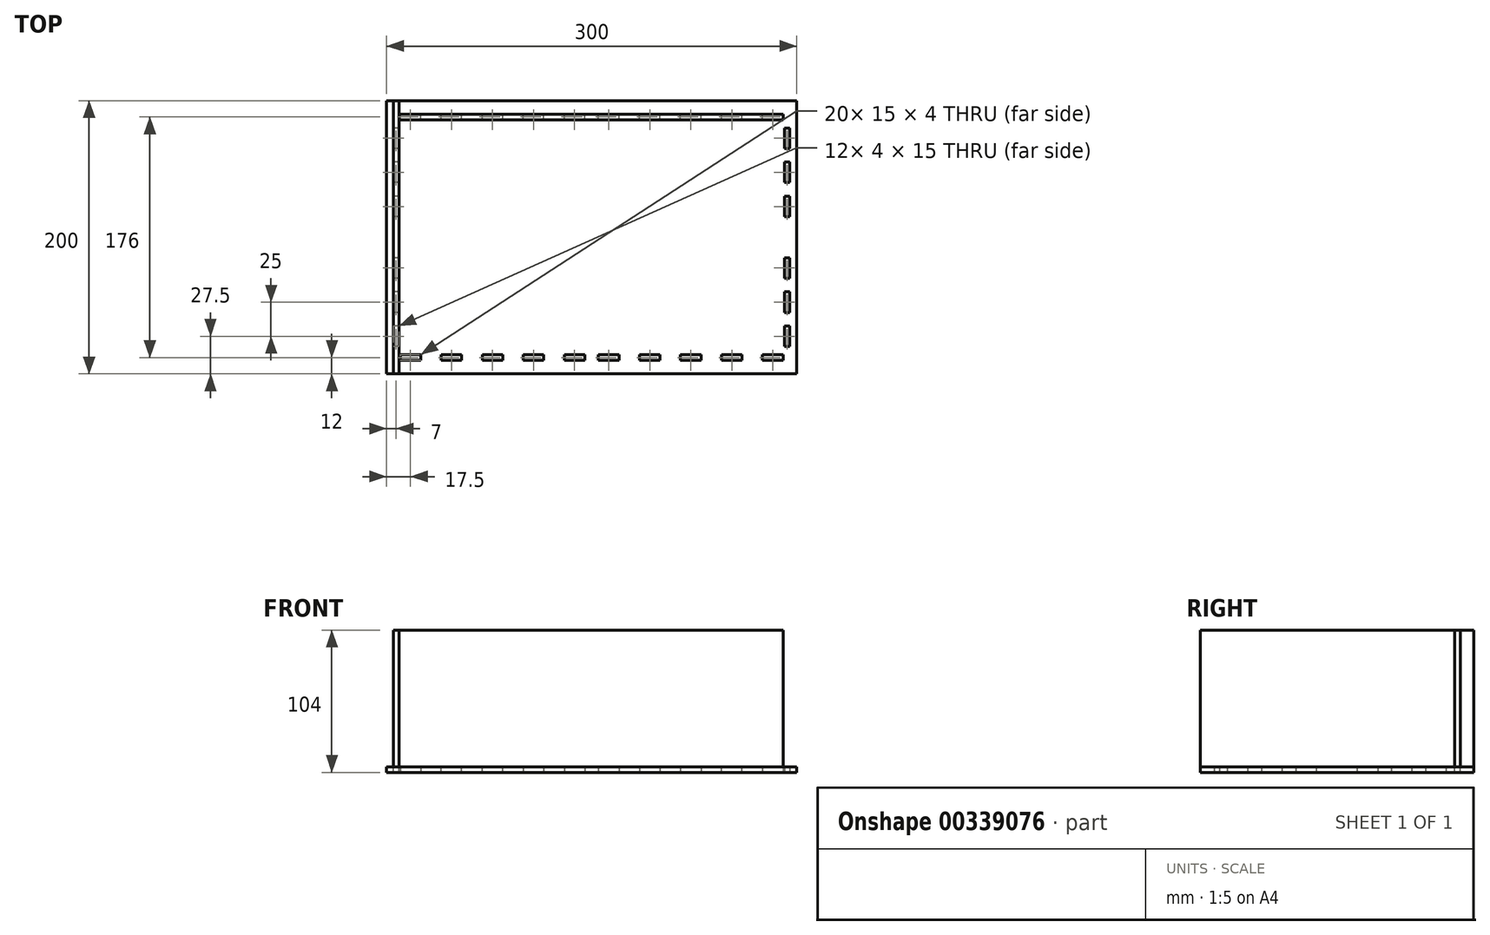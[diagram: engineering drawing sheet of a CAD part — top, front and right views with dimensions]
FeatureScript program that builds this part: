
annotation { "Feature Type Name" : "Feature", "Feature Type Description" : "" }
export const myFeature = defineFeature(function(context is Context, id is Id, definition is map)
    precondition{}
    {
        {
            assignVariable(context, id + "F0", {"name" : "material_thickness", "anyValue" : 4});
        }
        {
            var Q0;
            Q0=qCreatedBy(makeId("Top.planeOp"),FACE);
            var sketch = newSketch(context, id + "F1", { "sketchPlane" : qUnion([Q0])});
            skLineSegment(sketch, "E0.bottom", {"start": v(150, -100) * mm, "end": v(-150, -100) * mm});
            skLineSegment(sketch, "E0.top", {"start": v(150, 100) * mm, "end": v(-150, 100) * mm});
            skLineSegment(sketch, "E0.left", {"start": v(150, -100) * mm, "end": v(150, 100) * mm});
            skLineSegment(sketch, "E0.right", {"start": v(-150, -100) * mm, "end": v(-150, 100) * mm});
            skPoint(sketch, "E0.middle", {"position": v(0, 0) * mm});
            skLineSegment(sketch, "E1", {"start": v(0, 176.5) * mm, "end": v(0, -168.45) * mm, "construction": true});
            skPoint(sketch, "E1.endSnap0", {"position": v(0, -100) * mm});
            skLineSegment(sketch, "E2", {"start": v(-207.53, 0) * mm, "end": v(211.83, 0) * mm, "construction": true});
            skPoint(sketch, "E2.endSnap0", {"position": v(150, 0) * mm});
            skLineSegment(sketch, "E3.bottom", {"start": v(-125, 86) * mm, "end": v(-140, 86) * mm});
            skLineSegment(sketch, "E3.top", {"start": v(-125, 90) * mm, "end": v(-140, 90) * mm});
            skLineSegment(sketch, "E3.left", {"start": v(-125, 86) * mm, "end": v(-125, 90) * mm});
            skLineSegment(sketch, "E3.right", {"start": v(-140, 86) * mm, "end": v(-140, 90) * mm});
            skLineSegment(sketch, "E4.1.0.0", {"start": v(-95, 90) * mm, "end": v(-110, 90) * mm});
            skLineSegment(sketch, "E4.1.0.1", {"start": v(-110, 86) * mm, "end": v(-110, 90) * mm});
            skLineSegment(sketch, "E4.1.0.2", {"start": v(-95, 86) * mm, "end": v(-110, 86) * mm});
            skLineSegment(sketch, "E4.1.0.3", {"start": v(-95, 86) * mm, "end": v(-95, 90) * mm});
            skLineSegment(sketch, "E4.2.0.0", {"start": v(-65, 90) * mm, "end": v(-80, 90) * mm});
            skLineSegment(sketch, "E4.2.0.1", {"start": v(-80, 86) * mm, "end": v(-80, 90) * mm});
            skLineSegment(sketch, "E4.2.0.2", {"start": v(-65, 86) * mm, "end": v(-80, 86) * mm});
            skLineSegment(sketch, "E4.2.0.3", {"start": v(-65, 86) * mm, "end": v(-65, 90) * mm});
            skLineSegment(sketch, "E4.3.0.0", {"start": v(-35, 90) * mm, "end": v(-50, 90) * mm});
            skLineSegment(sketch, "E4.3.0.1", {"start": v(-50, 86) * mm, "end": v(-50, 90) * mm});
            skLineSegment(sketch, "E4.3.0.2", {"start": v(-35, 86) * mm, "end": v(-50, 86) * mm});
            skLineSegment(sketch, "E4.3.0.3", {"start": v(-35, 86) * mm, "end": v(-35, 90) * mm});
            skLineSegment(sketch, "E4.4.0.0", {"start": v(-5, 90) * mm, "end": v(-20, 90) * mm});
            skLineSegment(sketch, "E4.4.0.1", {"start": v(-20, 86) * mm, "end": v(-20, 90) * mm});
            skLineSegment(sketch, "E4.4.0.2", {"start": v(-5, 86) * mm, "end": v(-20, 86) * mm});
            skLineSegment(sketch, "E4.4.0.3", {"start": v(-5, 86) * mm, "end": v(-5, 90) * mm});
            skLineSegment(sketch, "E4.direction1", {"start": v(-140, 90) * mm, "end": v(-110, 90) * mm, "construction": true});
            skLineSegment(sketch, "E5.MirrorCS", {"start": v(5, 90) * mm, "end": v(20, 90) * mm});
            skLineSegment(sketch, "E6.MirrorCS", {"start": v(5, 86) * mm, "end": v(20, 86) * mm});
            skLineSegment(sketch, "E7.MirrorCS", {"start": v(5, 86) * mm, "end": v(5, 90) * mm});
            skLineSegment(sketch, "E8.MirrorCS", {"start": v(20, 86) * mm, "end": v(20, 90) * mm});
            skLineSegment(sketch, "E9.MirrorCS", {"start": v(110, 86) * mm, "end": v(110, 90) * mm});
            skLineSegment(sketch, "E10.MirrorCS", {"start": v(125, 86) * mm, "end": v(125, 90) * mm});
            skLineSegment(sketch, "E11.MirrorCS", {"start": v(50, 86) * mm, "end": v(50, 90) * mm});
            skLineSegment(sketch, "E12.MirrorCS", {"start": v(140, 86) * mm, "end": v(140, 90) * mm});
            skLineSegment(sketch, "E13.MirrorCS", {"start": v(95, 86) * mm, "end": v(95, 90) * mm});
            skLineSegment(sketch, "E14.MirrorCS", {"start": v(35, 86) * mm, "end": v(35, 90) * mm});
            skLineSegment(sketch, "E15.MirrorCS", {"start": v(80, 86) * mm, "end": v(80, 90) * mm});
            skLineSegment(sketch, "E16.MirrorCS", {"start": v(65, 86) * mm, "end": v(65, 90) * mm});
            skLineSegment(sketch, "E17.MirrorCS", {"start": v(125, 90) * mm, "end": v(140, 90) * mm});
            skLineSegment(sketch, "E18.MirrorCS", {"start": v(35, 86) * mm, "end": v(50, 86) * mm});
            skLineSegment(sketch, "E19.MirrorCS", {"start": v(95, 90) * mm, "end": v(110, 90) * mm});
            skLineSegment(sketch, "E20.MirrorCS", {"start": v(65, 86) * mm, "end": v(80, 86) * mm});
            skLineSegment(sketch, "E21.MirrorCS", {"start": v(95, 86) * mm, "end": v(110, 86) * mm});
            skLineSegment(sketch, "E22.MirrorCS", {"start": v(140, 90) * mm, "end": v(110, 90) * mm, "construction": true});
            skLineSegment(sketch, "E23.MirrorCS", {"start": v(65, 90) * mm, "end": v(80, 90) * mm});
            skLineSegment(sketch, "E24.MirrorCS", {"start": v(125, 86) * mm, "end": v(140, 86) * mm});
            skLineSegment(sketch, "E25.MirrorCS", {"start": v(35, 90) * mm, "end": v(50, 90) * mm});
            skLineSegment(sketch, "E26.bottom", {"start": v(141, 80) * mm, "end": v(145, 80) * mm});
            skLineSegment(sketch, "E26.top", {"start": v(141, 65) * mm, "end": v(145, 65) * mm});
            skLineSegment(sketch, "E26.left", {"start": v(141, 80) * mm, "end": v(141, 65) * mm});
            skLineSegment(sketch, "E26.right", {"start": v(145, 80) * mm, "end": v(145, 65) * mm});
            skLineSegment(sketch, "E27.0.1.0", {"start": v(145, 55) * mm, "end": v(145, 40) * mm});
            skLineSegment(sketch, "E27.0.1.1", {"start": v(141, 55) * mm, "end": v(145, 55) * mm});
            skLineSegment(sketch, "E27.0.1.2", {"start": v(141, 55) * mm, "end": v(141, 40) * mm});
            skLineSegment(sketch, "E27.0.1.3", {"start": v(141, 40) * mm, "end": v(145, 40) * mm});
            skLineSegment(sketch, "E27.0.2.0", {"start": v(145, 30) * mm, "end": v(145, 15) * mm});
            skLineSegment(sketch, "E27.0.2.1", {"start": v(141, 30) * mm, "end": v(145, 30) * mm});
            skLineSegment(sketch, "E27.0.2.2", {"start": v(141, 30) * mm, "end": v(141, 15) * mm});
            skLineSegment(sketch, "E27.0.2.3", {"start": v(141, 15) * mm, "end": v(145, 15) * mm});
            skLineSegment(sketch, "E27.direction1", {"start": v(145, 65) * mm, "end": v(170, 65) * mm, "construction": true});
            skLineSegment(sketch, "E27.direction2", {"start": v(145, 65) * mm, "end": v(145, 40) * mm, "construction": true});
            skLineSegment(sketch, "E28.MirrorCS", {"start": v(141, -55) * mm, "end": v(141, -40) * mm});
            skLineSegment(sketch, "E29.MirrorCS", {"start": v(141, -40) * mm, "end": v(145, -40) * mm});
            skLineSegment(sketch, "E30.MirrorCS", {"start": v(141, -30) * mm, "end": v(145, -30) * mm});
            skLineSegment(sketch, "E31.MirrorCS", {"start": v(145, -30) * mm, "end": v(145, -15) * mm});
            skLineSegment(sketch, "E32.MirrorCS", {"start": v(141, -30) * mm, "end": v(141, -15) * mm});
            skLineSegment(sketch, "E33.MirrorCS", {"start": v(141, -15) * mm, "end": v(145, -15) * mm});
            skLineSegment(sketch, "E34.MirrorCS", {"start": v(141, -55) * mm, "end": v(145, -55) * mm});
            skLineSegment(sketch, "E35.MirrorCS", {"start": v(141, -65) * mm, "end": v(145, -65) * mm});
            skLineSegment(sketch, "E36.MirrorCS", {"start": v(145, -80) * mm, "end": v(145, -65) * mm});
            skLineSegment(sketch, "E37.MirrorCS", {"start": v(141, -80) * mm, "end": v(141, -65) * mm});
            skLineSegment(sketch, "E38.MirrorCS", {"start": v(141, -80) * mm, "end": v(145, -80) * mm});
            skLineSegment(sketch, "E39.MirrorCS", {"start": v(145, -55) * mm, "end": v(145, -40) * mm});
            skLineSegment(sketch, "E40.MirrorCS", {"start": v(140, -86) * mm, "end": v(140, -90) * mm});
            skLineSegment(sketch, "E41.MirrorCS", {"start": v(125, -86) * mm, "end": v(140, -86) * mm});
            skLineSegment(sketch, "E42.MirrorCS", {"start": v(125, -86) * mm, "end": v(125, -90) * mm});
            skLineSegment(sketch, "E43.MirrorCS", {"start": v(125, -90) * mm, "end": v(140, -90) * mm});
            skLineSegment(sketch, "E44.MirrorCS", {"start": v(110, -86) * mm, "end": v(110, -90) * mm});
            skLineSegment(sketch, "E45.MirrorCS", {"start": v(95, -90) * mm, "end": v(110, -90) * mm});
            skLineSegment(sketch, "E46.MirrorCS", {"start": v(95, -86) * mm, "end": v(95, -90) * mm});
            skLineSegment(sketch, "E47.MirrorCS", {"start": v(95, -86) * mm, "end": v(110, -86) * mm});
            skLineSegment(sketch, "E48.MirrorCS", {"start": v(80, -86) * mm, "end": v(80, -90) * mm});
            skLineSegment(sketch, "E49.MirrorCS", {"start": v(65, -90) * mm, "end": v(80, -90) * mm});
            skLineSegment(sketch, "E50.MirrorCS", {"start": v(65, -86) * mm, "end": v(65, -90) * mm});
            skLineSegment(sketch, "E51.MirrorCS", {"start": v(65, -86) * mm, "end": v(80, -86) * mm});
            skLineSegment(sketch, "E52.MirrorCS", {"start": v(50, -86) * mm, "end": v(50, -90) * mm});
            skLineSegment(sketch, "E53.MirrorCS", {"start": v(35, -90) * mm, "end": v(50, -90) * mm});
            skLineSegment(sketch, "E54.MirrorCS", {"start": v(35, -86) * mm, "end": v(50, -86) * mm});
            skLineSegment(sketch, "E55.MirrorCS", {"start": v(35, -86) * mm, "end": v(35, -90) * mm});
            skLineSegment(sketch, "E56.MirrorCS", {"start": v(20, -86) * mm, "end": v(20, -90) * mm});
            skLineSegment(sketch, "E57.MirrorCS", {"start": v(5, -90) * mm, "end": v(20, -90) * mm});
            skLineSegment(sketch, "E58.MirrorCS", {"start": v(5, -86) * mm, "end": v(20, -86) * mm});
            skLineSegment(sketch, "E59.MirrorCS", {"start": v(5, -86) * mm, "end": v(5, -90) * mm});
            skLineSegment(sketch, "E60.MirrorCS", {"start": v(-5, -86) * mm, "end": v(-5, -90) * mm});
            skLineSegment(sketch, "E61.MirrorCS", {"start": v(-5, -90) * mm, "end": v(-20, -90) * mm});
            skLineSegment(sketch, "E62.MirrorCS", {"start": v(-5, -86) * mm, "end": v(-20, -86) * mm});
            skLineSegment(sketch, "E63.MirrorCS", {"start": v(-20, -86) * mm, "end": v(-20, -90) * mm});
            skLineSegment(sketch, "E64.MirrorCS", {"start": v(-35, -86) * mm, "end": v(-35, -90) * mm});
            skLineSegment(sketch, "E65.MirrorCS", {"start": v(-35, -90) * mm, "end": v(-50, -90) * mm});
            skLineSegment(sketch, "E66.MirrorCS", {"start": v(-35, -86) * mm, "end": v(-50, -86) * mm});
            skLineSegment(sketch, "E67.MirrorCS", {"start": v(-50, -86) * mm, "end": v(-50, -90) * mm});
            skLineSegment(sketch, "E68.MirrorCS", {"start": v(-65, -86) * mm, "end": v(-65, -90) * mm});
            skLineSegment(sketch, "E69.MirrorCS", {"start": v(-65, -90) * mm, "end": v(-80, -90) * mm});
            skLineSegment(sketch, "E70.MirrorCS", {"start": v(-65, -86) * mm, "end": v(-80, -86) * mm});
            skLineSegment(sketch, "E71.MirrorCS", {"start": v(-80, -86) * mm, "end": v(-80, -90) * mm});
            skLineSegment(sketch, "E72.MirrorCS", {"start": v(-95, -86) * mm, "end": v(-95, -90) * mm});
            skLineSegment(sketch, "E73.MirrorCS", {"start": v(-95, -90) * mm, "end": v(-110, -90) * mm});
            skLineSegment(sketch, "E74.MirrorCS", {"start": v(-95, -86) * mm, "end": v(-110, -86) * mm});
            skLineSegment(sketch, "E75.MirrorCS", {"start": v(-110, -86) * mm, "end": v(-110, -90) * mm});
            skLineSegment(sketch, "E76.MirrorCS", {"start": v(-125, -86) * mm, "end": v(-125, -90) * mm});
            skLineSegment(sketch, "E77.MirrorCS", {"start": v(-125, -86) * mm, "end": v(-140, -86) * mm});
            skLineSegment(sketch, "E78.MirrorCS", {"start": v(-140, -86) * mm, "end": v(-140, -90) * mm});
            skLineSegment(sketch, "E79.MirrorCS", {"start": v(-125, -90) * mm, "end": v(-140, -90) * mm});
            skLineSegment(sketch, "E80.MirrorCS", {"start": v(-141, 80) * mm, "end": v(-145, 80) * mm});
            skLineSegment(sketch, "E81.MirrorCS", {"start": v(-141, 80) * mm, "end": v(-141, 65) * mm});
            skLineSegment(sketch, "E82.MirrorCS", {"start": v(-145, 80) * mm, "end": v(-145, 65) * mm});
            skLineSegment(sketch, "E83.MirrorCS", {"start": v(-141, 65) * mm, "end": v(-145, 65) * mm});
            skLineSegment(sketch, "E84.MirrorCS", {"start": v(-141, 55) * mm, "end": v(-141, 40) * mm});
            skLineSegment(sketch, "E85.MirrorCS", {"start": v(-141, 40) * mm, "end": v(-145, 40) * mm});
            skLineSegment(sketch, "E86.MirrorCS", {"start": v(-141, 55) * mm, "end": v(-145, 55) * mm});
            skLineSegment(sketch, "E87.MirrorCS", {"start": v(-145, 55) * mm, "end": v(-145, 40) * mm});
            skLineSegment(sketch, "E88.MirrorCS", {"start": v(-141, 30) * mm, "end": v(-145, 30) * mm});
            skLineSegment(sketch, "E89.MirrorCS", {"start": v(-141, 30) * mm, "end": v(-141, 15) * mm});
            skLineSegment(sketch, "E90.MirrorCS", {"start": v(-145, 30) * mm, "end": v(-145, 15) * mm});
            skLineSegment(sketch, "E91.MirrorCS", {"start": v(-141, 15) * mm, "end": v(-145, 15) * mm});
            skLineSegment(sketch, "E92.MirrorCS", {"start": v(-141, -30) * mm, "end": v(-141, -15) * mm});
            skLineSegment(sketch, "E93.MirrorCS", {"start": v(-145, -30) * mm, "end": v(-145, -15) * mm});
            skLineSegment(sketch, "E94.MirrorCS", {"start": v(-141, -30) * mm, "end": v(-145, -30) * mm});
            skLineSegment(sketch, "E95.MirrorCS", {"start": v(-141, -15) * mm, "end": v(-145, -15) * mm});
            skLineSegment(sketch, "E96.MirrorCS", {"start": v(-145, -55) * mm, "end": v(-145, -40) * mm});
            skLineSegment(sketch, "E97.MirrorCS", {"start": v(-141, -55) * mm, "end": v(-141, -40) * mm});
            skLineSegment(sketch, "E98.MirrorCS", {"start": v(-141, -55) * mm, "end": v(-145, -55) * mm});
            skLineSegment(sketch, "E99.MirrorCS", {"start": v(-141, -40) * mm, "end": v(-145, -40) * mm});
            skLineSegment(sketch, "E100.MirrorCS", {"start": v(-141, -65) * mm, "end": v(-145, -65) * mm});
            skLineSegment(sketch, "E101.MirrorCS", {"start": v(-141, -80) * mm, "end": v(-141, -65) * mm});
            skLineSegment(sketch, "E102.MirrorCS", {"start": v(-145, -80) * mm, "end": v(-145, -65) * mm});
            skLineSegment(sketch, "E103.MirrorCS", {"start": v(-141, -80) * mm, "end": v(-145, -80) * mm});
            skSolve(sketch);
        }
        {
            var Q0;
            Q0=makeQuery(id+"F1.imprint","IMPRINT",FACE,{"disambiguationData":[TD([[makeQuery(id+"F1.imprint","IMPRINT",EDGE,{"derivedFrom":sQuery(id+"F1.wireOp",EDGE,"E0.bottom")}),-1.0]])]});
            extrude(context, id + "F2", {"entities" : qUnion([Q0]), "depth" : (getVariable(context, 'material_thickness')) * mm});
        }
        {
            var Q0;
            Q0=makeQuery(id+"F2.opExtrude","CAP_FACE",FACE,{"disambiguationData":[OSD([sQuery(id+"F1.wireOp",EDGE,"E0.bottom"),sQuery(id+"F1.wireOp",EDGE,"E0.top"),sQuery(id+"F1.wireOp",EDGE,"E0.left"),sQuery(id+"F1.wireOp",EDGE,"E0.right"),sQuery(id+"F1.wireOp",EDGE,"E3.bottom"),sQuery(id+"F1.wireOp",EDGE,"E3.top"),sQuery(id+"F1.wireOp",EDGE,"E3.left"),sQuery(id+"F1.wireOp",EDGE,"E3.right"),sQuery(id+"F1.wireOp",EDGE,"E4.1.0.0"),sQuery(id+"F1.wireOp",EDGE,"E4.1.0.1"),sQuery(id+"F1.wireOp",EDGE,"E4.1.0.2"),sQuery(id+"F1.wireOp",EDGE,"E4.1.0.3"),sQuery(id+"F1.wireOp",EDGE,"E4.2.0.0"),sQuery(id+"F1.wireOp",EDGE,"E4.2.0.1"),sQuery(id+"F1.wireOp",EDGE,"E4.2.0.2"),sQuery(id+"F1.wireOp",EDGE,"E4.2.0.3"),sQuery(id+"F1.wireOp",EDGE,"E4.3.0.0"),sQuery(id+"F1.wireOp",EDGE,"E4.3.0.1"),sQuery(id+"F1.wireOp",EDGE,"E4.3.0.2"),sQuery(id+"F1.wireOp",EDGE,"E4.3.0.3"),sQuery(id+"F1.wireOp",EDGE,"E4.4.0.0"),sQuery(id+"F1.wireOp",EDGE,"E4.4.0.1"),sQuery(id+"F1.wireOp",EDGE,"E4.4.0.2"),sQuery(id+"F1.wireOp",EDGE,"E4.4.0.3"),sQuery(id+"F1.wireOp",EDGE,"E5.MirrorCS"),sQuery(id+"F1.wireOp",EDGE,"E6.MirrorCS"),sQuery(id+"F1.wireOp",EDGE,"E7.MirrorCS"),sQuery(id+"F1.wireOp",EDGE,"E8.MirrorCS"),sQuery(id+"F1.wireOp",EDGE,"E9.MirrorCS"),sQuery(id+"F1.wireOp",EDGE,"E10.MirrorCS"),sQuery(id+"F1.wireOp",EDGE,"E11.MirrorCS"),sQuery(id+"F1.wireOp",EDGE,"E12.MirrorCS"),sQuery(id+"F1.wireOp",EDGE,"E13.MirrorCS"),sQuery(id+"F1.wireOp",EDGE,"E14.MirrorCS"),sQuery(id+"F1.wireOp",EDGE,"E15.MirrorCS"),sQuery(id+"F1.wireOp",EDGE,"E16.MirrorCS"),sQuery(id+"F1.wireOp",EDGE,"E17.MirrorCS"),sQuery(id+"F1.wireOp",EDGE,"E18.MirrorCS"),sQuery(id+"F1.wireOp",EDGE,"E19.MirrorCS"),sQuery(id+"F1.wireOp",EDGE,"E20.MirrorCS"),sQuery(id+"F1.wireOp",EDGE,"E21.MirrorCS"),sQuery(id+"F1.wireOp",EDGE,"E23.MirrorCS"),sQuery(id+"F1.wireOp",EDGE,"E24.MirrorCS"),sQuery(id+"F1.wireOp",EDGE,"E25.MirrorCS"),sQuery(id+"F1.wireOp",EDGE,"E26.bottom"),sQuery(id+"F1.wireOp",EDGE,"E26.top"),sQuery(id+"F1.wireOp",EDGE,"E26.left"),sQuery(id+"F1.wireOp",EDGE,"E26.right"),sQuery(id+"F1.wireOp",EDGE,"E27.0.1.0"),sQuery(id+"F1.wireOp",EDGE,"E27.0.1.1"),sQuery(id+"F1.wireOp",EDGE,"E27.0.1.2"),sQuery(id+"F1.wireOp",EDGE,"E27.0.1.3"),sQuery(id+"F1.wireOp",EDGE,"E27.0.2.0"),sQuery(id+"F1.wireOp",EDGE,"E27.0.2.1"),sQuery(id+"F1.wireOp",EDGE,"E27.0.2.2"),sQuery(id+"F1.wireOp",EDGE,"E27.0.2.3"),sQuery(id+"F1.wireOp",EDGE,"E28.MirrorCS"),sQuery(id+"F1.wireOp",EDGE,"E30.MirrorCS"),sQuery(id+"F1.wireOp",EDGE,"E31.MirrorCS"),sQuery(id+"F1.wireOp",EDGE,"E32.MirrorCS"),sQuery(id+"F1.wireOp",EDGE,"E33.MirrorCS"),sQuery(id+"F1.wireOp",EDGE,"E29.MirrorCS"),sQuery(id+"F1.wireOp",EDGE,"E34.MirrorCS"),sQuery(id+"F1.wireOp",EDGE,"E35.MirrorCS"),sQuery(id+"F1.wireOp",EDGE,"E36.MirrorCS"),sQuery(id+"F1.wireOp",EDGE,"E37.MirrorCS"),sQuery(id+"F1.wireOp",EDGE,"E38.MirrorCS"),sQuery(id+"F1.wireOp",EDGE,"E39.MirrorCS"),sQuery(id+"F1.wireOp",EDGE,"E40.MirrorCS"),sQuery(id+"F1.wireOp",EDGE,"E41.MirrorCS"),sQuery(id+"F1.wireOp",EDGE,"E42.MirrorCS"),sQuery(id+"F1.wireOp",EDGE,"E43.MirrorCS"),sQuery(id+"F1.wireOp",EDGE,"E44.MirrorCS"),sQuery(id+"F1.wireOp",EDGE,"E45.MirrorCS"),sQuery(id+"F1.wireOp",EDGE,"E46.MirrorCS"),sQuery(id+"F1.wireOp",EDGE,"E47.MirrorCS"),sQuery(id+"F1.wireOp",EDGE,"E48.MirrorCS"),sQuery(id+"F1.wireOp",EDGE,"E49.MirrorCS"),sQuery(id+"F1.wireOp",EDGE,"E50.MirrorCS"),sQuery(id+"F1.wireOp",EDGE,"E51.MirrorCS"),sQuery(id+"F1.wireOp",EDGE,"E52.MirrorCS"),sQuery(id+"F1.wireOp",EDGE,"E53.MirrorCS"),sQuery(id+"F1.wireOp",EDGE,"E54.MirrorCS"),sQuery(id+"F1.wireOp",EDGE,"E55.MirrorCS"),sQuery(id+"F1.wireOp",EDGE,"E56.MirrorCS"),sQuery(id+"F1.wireOp",EDGE,"E57.MirrorCS"),sQuery(id+"F1.wireOp",EDGE,"E58.MirrorCS"),sQuery(id+"F1.wireOp",EDGE,"E59.MirrorCS"),sQuery(id+"F1.wireOp",EDGE,"E60.MirrorCS"),sQuery(id+"F1.wireOp",EDGE,"E61.MirrorCS"),sQuery(id+"F1.wireOp",EDGE,"E62.MirrorCS"),sQuery(id+"F1.wireOp",EDGE,"E63.MirrorCS"),sQuery(id+"F1.wireOp",EDGE,"E64.MirrorCS"),sQuery(id+"F1.wireOp",EDGE,"E65.MirrorCS"),sQuery(id+"F1.wireOp",EDGE,"E66.MirrorCS"),sQuery(id+"F1.wireOp",EDGE,"E67.MirrorCS"),sQuery(id+"F1.wireOp",EDGE,"E68.MirrorCS"),sQuery(id+"F1.wireOp",EDGE,"E69.MirrorCS"),sQuery(id+"F1.wireOp",EDGE,"E70.MirrorCS"),sQuery(id+"F1.wireOp",EDGE,"E71.MirrorCS"),sQuery(id+"F1.wireOp",EDGE,"E72.MirrorCS"),sQuery(id+"F1.wireOp",EDGE,"E73.MirrorCS"),sQuery(id+"F1.wireOp",EDGE,"E74.MirrorCS"),sQuery(id+"F1.wireOp",EDGE,"E75.MirrorCS"),sQuery(id+"F1.wireOp",EDGE,"E76.MirrorCS"),sQuery(id+"F1.wireOp",EDGE,"E77.MirrorCS"),sQuery(id+"F1.wireOp",EDGE,"E78.MirrorCS"),sQuery(id+"F1.wireOp",EDGE,"E79.MirrorCS"),sQuery(id+"F1.wireOp",EDGE,"E80.MirrorCS"),sQuery(id+"F1.wireOp",EDGE,"E81.MirrorCS"),sQuery(id+"F1.wireOp",EDGE,"E82.MirrorCS"),sQuery(id+"F1.wireOp",EDGE,"E83.MirrorCS"),sQuery(id+"F1.wireOp",EDGE,"E84.MirrorCS"),sQuery(id+"F1.wireOp",EDGE,"E85.MirrorCS"),sQuery(id+"F1.wireOp",EDGE,"E86.MirrorCS"),sQuery(id+"F1.wireOp",EDGE,"E87.MirrorCS"),sQuery(id+"F1.wireOp",EDGE,"E88.MirrorCS"),sQuery(id+"F1.wireOp",EDGE,"E89.MirrorCS"),sQuery(id+"F1.wireOp",EDGE,"E90.MirrorCS"),sQuery(id+"F1.wireOp",EDGE,"E91.MirrorCS"),sQuery(id+"F1.wireOp",EDGE,"E92.MirrorCS"),sQuery(id+"F1.wireOp",EDGE,"E93.MirrorCS"),sQuery(id+"F1.wireOp",EDGE,"E94.MirrorCS"),sQuery(id+"F1.wireOp",EDGE,"E95.MirrorCS"),sQuery(id+"F1.wireOp",EDGE,"E96.MirrorCS"),sQuery(id+"F1.wireOp",EDGE,"E97.MirrorCS"),sQuery(id+"F1.wireOp",EDGE,"E98.MirrorCS"),sQuery(id+"F1.wireOp",EDGE,"E99.MirrorCS"),sQuery(id+"F1.wireOp",EDGE,"E100.MirrorCS"),sQuery(id+"F1.wireOp",EDGE,"E101.MirrorCS"),sQuery(id+"F1.wireOp",EDGE,"E102.MirrorCS"),sQuery(id+"F1.wireOp",EDGE,"E103.MirrorCS")])],"isStart":false});
            var sketch = newSketch(context, id + "F3", { "sketchPlane" : qUnion([Q0])});
            skLineSegment(sketch, "E104.bottom", {"start": v(-145, -80) * mm, "end": v(-141, -80) * mm});
            skLineSegment(sketch, "E104.top", {"start": v(-145, -65) * mm, "end": v(-141, -65) * mm});
            skLineSegment(sketch, "E104.left", {"start": v(-145, -80) * mm, "end": v(-145, -65) * mm});
            skLineSegment(sketch, "E104.right", {"start": v(-141, -80) * mm, "end": v(-141, -65) * mm});
            skLineSegment(sketch, "E105.bottom", {"start": v(-145, -55) * mm, "end": v(-141, -55) * mm});
            skLineSegment(sketch, "E105.top", {"start": v(-145, -40) * mm, "end": v(-141, -40) * mm});
            skLineSegment(sketch, "E105.left", {"start": v(-145, -55) * mm, "end": v(-145, -40) * mm});
            skLineSegment(sketch, "E105.right", {"start": v(-141, -55) * mm, "end": v(-141, -40) * mm});
            skLineSegment(sketch, "E106.bottom", {"start": v(-145, -30) * mm, "end": v(-141, -30) * mm});
            skLineSegment(sketch, "E106.top", {"start": v(-145, -15) * mm, "end": v(-141, -15) * mm});
            skLineSegment(sketch, "E106.left", {"start": v(-145, -30) * mm, "end": v(-145, -15) * mm});
            skLineSegment(sketch, "E106.right", {"start": v(-141, -30) * mm, "end": v(-141, -15) * mm});
            skLineSegment(sketch, "E107.bottom", {"start": v(-145, 15) * mm, "end": v(-141, 15) * mm});
            skLineSegment(sketch, "E107.top", {"start": v(-145, 30) * mm, "end": v(-141, 30) * mm});
            skLineSegment(sketch, "E107.left", {"start": v(-145, 15) * mm, "end": v(-145, 30) * mm});
            skLineSegment(sketch, "E107.right", {"start": v(-141, 15) * mm, "end": v(-141, 30) * mm});
            skLineSegment(sketch, "E108.bottom", {"start": v(-145, 40) * mm, "end": v(-141, 40) * mm});
            skLineSegment(sketch, "E108.top", {"start": v(-145, 55) * mm, "end": v(-141, 55) * mm});
            skLineSegment(sketch, "E108.left", {"start": v(-145, 40) * mm, "end": v(-145, 55) * mm});
            skLineSegment(sketch, "E108.right", {"start": v(-141, 40) * mm, "end": v(-141, 55) * mm});
            skLineSegment(sketch, "E109.bottom", {"start": v(-145, 65) * mm, "end": v(-141, 65) * mm});
            skLineSegment(sketch, "E109.top", {"start": v(-145, 80) * mm, "end": v(-141, 80) * mm});
            skLineSegment(sketch, "E109.left", {"start": v(-145, 65) * mm, "end": v(-145, 80) * mm});
            skLineSegment(sketch, "E109.right", {"start": v(-141, 65) * mm, "end": v(-141, 80) * mm});
            skSolve(sketch);
        }
        {
            var Q0;
            Q0=makeQuery(id+"F3.imprint","IMPRINT",FACE,{"disambiguationData":[TD([[makeQuery(id+"F3.imprint","IMPRINT",EDGE,{"derivedFrom":sQuery(id+"F3.wireOp",EDGE,"E104.bottom")}),-1.0]])]});
            var Q1;
            Q1=makeQuery(id+"F3.imprint","IMPRINT",FACE,{"disambiguationData":[TD([[makeQuery(id+"F3.imprint","IMPRINT",EDGE,{"derivedFrom":sQuery(id+"F3.wireOp",EDGE,"E105.bottom")}),-1.0]])]});
            var Q2;
            Q2=makeQuery(id+"F3.imprint","IMPRINT",FACE,{"disambiguationData":[TD([[makeQuery(id+"F3.imprint","IMPRINT",EDGE,{"derivedFrom":sQuery(id+"F3.wireOp",EDGE,"E106.bottom")}),-1.0]])]});
            var Q3;
            Q3=makeQuery(id+"F3.imprint","IMPRINT",FACE,{"disambiguationData":[TD([[makeQuery(id+"F3.imprint","IMPRINT",EDGE,{"derivedFrom":sQuery(id+"F3.wireOp",EDGE,"E107.bottom")}),-1.0]])]});
            var Q4;
            Q4=makeQuery(id+"F3.imprint","IMPRINT",FACE,{"disambiguationData":[TD([[makeQuery(id+"F3.imprint","IMPRINT",EDGE,{"derivedFrom":sQuery(id+"F3.wireOp",EDGE,"E108.bottom")}),-1.0]])]});
            var Q5;
            Q5=makeQuery(id+"F3.imprint","IMPRINT",FACE,{"disambiguationData":[TD([[makeQuery(id+"F3.imprint","IMPRINT",EDGE,{"derivedFrom":sQuery(id+"F3.wireOp",EDGE,"E109.bottom")}),-1.0]])]});
            extrude(context, id + "F4", {"entities" : qUnion([Q0, Q1, Q2, Q3, Q4, Q5]), "oppositeDirection" : true, "depth" : 4 * mm});
        }
        {
            var Q0;
            Q0=makeQuery(id+"F2.opExtrude","CAP_FACE",FACE,{"disambiguationData":[OSD([sQuery(id+"F1.wireOp",EDGE,"E0.bottom"),sQuery(id+"F1.wireOp",EDGE,"E0.top"),sQuery(id+"F1.wireOp",EDGE,"E0.left"),sQuery(id+"F1.wireOp",EDGE,"E0.right"),sQuery(id+"F1.wireOp",EDGE,"E3.bottom"),sQuery(id+"F1.wireOp",EDGE,"E3.top"),sQuery(id+"F1.wireOp",EDGE,"E3.left"),sQuery(id+"F1.wireOp",EDGE,"E3.right"),sQuery(id+"F1.wireOp",EDGE,"E4.1.0.0"),sQuery(id+"F1.wireOp",EDGE,"E4.1.0.1"),sQuery(id+"F1.wireOp",EDGE,"E4.1.0.2"),sQuery(id+"F1.wireOp",EDGE,"E4.1.0.3"),sQuery(id+"F1.wireOp",EDGE,"E4.2.0.0"),sQuery(id+"F1.wireOp",EDGE,"E4.2.0.1"),sQuery(id+"F1.wireOp",EDGE,"E4.2.0.2"),sQuery(id+"F1.wireOp",EDGE,"E4.2.0.3"),sQuery(id+"F1.wireOp",EDGE,"E4.3.0.0"),sQuery(id+"F1.wireOp",EDGE,"E4.3.0.1"),sQuery(id+"F1.wireOp",EDGE,"E4.3.0.2"),sQuery(id+"F1.wireOp",EDGE,"E4.3.0.3"),sQuery(id+"F1.wireOp",EDGE,"E4.4.0.0"),sQuery(id+"F1.wireOp",EDGE,"E4.4.0.1"),sQuery(id+"F1.wireOp",EDGE,"E4.4.0.2"),sQuery(id+"F1.wireOp",EDGE,"E4.4.0.3"),sQuery(id+"F1.wireOp",EDGE,"E5.MirrorCS"),sQuery(id+"F1.wireOp",EDGE,"E6.MirrorCS"),sQuery(id+"F1.wireOp",EDGE,"E7.MirrorCS"),sQuery(id+"F1.wireOp",EDGE,"E8.MirrorCS"),sQuery(id+"F1.wireOp",EDGE,"E9.MirrorCS"),sQuery(id+"F1.wireOp",EDGE,"E10.MirrorCS"),sQuery(id+"F1.wireOp",EDGE,"E11.MirrorCS"),sQuery(id+"F1.wireOp",EDGE,"E12.MirrorCS"),sQuery(id+"F1.wireOp",EDGE,"E13.MirrorCS"),sQuery(id+"F1.wireOp",EDGE,"E14.MirrorCS"),sQuery(id+"F1.wireOp",EDGE,"E15.MirrorCS"),sQuery(id+"F1.wireOp",EDGE,"E16.MirrorCS"),sQuery(id+"F1.wireOp",EDGE,"E17.MirrorCS"),sQuery(id+"F1.wireOp",EDGE,"E18.MirrorCS"),sQuery(id+"F1.wireOp",EDGE,"E19.MirrorCS"),sQuery(id+"F1.wireOp",EDGE,"E20.MirrorCS"),sQuery(id+"F1.wireOp",EDGE,"E21.MirrorCS"),sQuery(id+"F1.wireOp",EDGE,"E23.MirrorCS"),sQuery(id+"F1.wireOp",EDGE,"E24.MirrorCS"),sQuery(id+"F1.wireOp",EDGE,"E25.MirrorCS"),sQuery(id+"F1.wireOp",EDGE,"E26.bottom"),sQuery(id+"F1.wireOp",EDGE,"E26.top"),sQuery(id+"F1.wireOp",EDGE,"E26.left"),sQuery(id+"F1.wireOp",EDGE,"E26.right"),sQuery(id+"F1.wireOp",EDGE,"E27.0.1.0"),sQuery(id+"F1.wireOp",EDGE,"E27.0.1.1"),sQuery(id+"F1.wireOp",EDGE,"E27.0.1.2"),sQuery(id+"F1.wireOp",EDGE,"E27.0.1.3"),sQuery(id+"F1.wireOp",EDGE,"E27.0.2.0"),sQuery(id+"F1.wireOp",EDGE,"E27.0.2.1"),sQuery(id+"F1.wireOp",EDGE,"E27.0.2.2"),sQuery(id+"F1.wireOp",EDGE,"E27.0.2.3"),sQuery(id+"F1.wireOp",EDGE,"E28.MirrorCS"),sQuery(id+"F1.wireOp",EDGE,"E30.MirrorCS"),sQuery(id+"F1.wireOp",EDGE,"E31.MirrorCS"),sQuery(id+"F1.wireOp",EDGE,"E32.MirrorCS"),sQuery(id+"F1.wireOp",EDGE,"E33.MirrorCS"),sQuery(id+"F1.wireOp",EDGE,"E29.MirrorCS"),sQuery(id+"F1.wireOp",EDGE,"E34.MirrorCS"),sQuery(id+"F1.wireOp",EDGE,"E35.MirrorCS"),sQuery(id+"F1.wireOp",EDGE,"E36.MirrorCS"),sQuery(id+"F1.wireOp",EDGE,"E37.MirrorCS"),sQuery(id+"F1.wireOp",EDGE,"E38.MirrorCS"),sQuery(id+"F1.wireOp",EDGE,"E39.MirrorCS"),sQuery(id+"F1.wireOp",EDGE,"E40.MirrorCS"),sQuery(id+"F1.wireOp",EDGE,"E41.MirrorCS"),sQuery(id+"F1.wireOp",EDGE,"E42.MirrorCS"),sQuery(id+"F1.wireOp",EDGE,"E43.MirrorCS"),sQuery(id+"F1.wireOp",EDGE,"E44.MirrorCS"),sQuery(id+"F1.wireOp",EDGE,"E45.MirrorCS"),sQuery(id+"F1.wireOp",EDGE,"E46.MirrorCS"),sQuery(id+"F1.wireOp",EDGE,"E47.MirrorCS"),sQuery(id+"F1.wireOp",EDGE,"E48.MirrorCS"),sQuery(id+"F1.wireOp",EDGE,"E49.MirrorCS"),sQuery(id+"F1.wireOp",EDGE,"E50.MirrorCS"),sQuery(id+"F1.wireOp",EDGE,"E51.MirrorCS"),sQuery(id+"F1.wireOp",EDGE,"E52.MirrorCS"),sQuery(id+"F1.wireOp",EDGE,"E53.MirrorCS"),sQuery(id+"F1.wireOp",EDGE,"E54.MirrorCS"),sQuery(id+"F1.wireOp",EDGE,"E55.MirrorCS"),sQuery(id+"F1.wireOp",EDGE,"E56.MirrorCS"),sQuery(id+"F1.wireOp",EDGE,"E57.MirrorCS"),sQuery(id+"F1.wireOp",EDGE,"E58.MirrorCS"),sQuery(id+"F1.wireOp",EDGE,"E59.MirrorCS"),sQuery(id+"F1.wireOp",EDGE,"E60.MirrorCS"),sQuery(id+"F1.wireOp",EDGE,"E61.MirrorCS"),sQuery(id+"F1.wireOp",EDGE,"E62.MirrorCS"),sQuery(id+"F1.wireOp",EDGE,"E63.MirrorCS"),sQuery(id+"F1.wireOp",EDGE,"E64.MirrorCS"),sQuery(id+"F1.wireOp",EDGE,"E65.MirrorCS"),sQuery(id+"F1.wireOp",EDGE,"E66.MirrorCS"),sQuery(id+"F1.wireOp",EDGE,"E67.MirrorCS"),sQuery(id+"F1.wireOp",EDGE,"E68.MirrorCS"),sQuery(id+"F1.wireOp",EDGE,"E69.MirrorCS"),sQuery(id+"F1.wireOp",EDGE,"E70.MirrorCS"),sQuery(id+"F1.wireOp",EDGE,"E71.MirrorCS"),sQuery(id+"F1.wireOp",EDGE,"E72.MirrorCS"),sQuery(id+"F1.wireOp",EDGE,"E73.MirrorCS"),sQuery(id+"F1.wireOp",EDGE,"E74.MirrorCS"),sQuery(id+"F1.wireOp",EDGE,"E75.MirrorCS"),sQuery(id+"F1.wireOp",EDGE,"E76.MirrorCS"),sQuery(id+"F1.wireOp",EDGE,"E77.MirrorCS"),sQuery(id+"F1.wireOp",EDGE,"E78.MirrorCS"),sQuery(id+"F1.wireOp",EDGE,"E79.MirrorCS"),sQuery(id+"F1.wireOp",EDGE,"E80.MirrorCS"),sQuery(id+"F1.wireOp",EDGE,"E81.MirrorCS"),sQuery(id+"F1.wireOp",EDGE,"E82.MirrorCS"),sQuery(id+"F1.wireOp",EDGE,"E83.MirrorCS"),sQuery(id+"F1.wireOp",EDGE,"E84.MirrorCS"),sQuery(id+"F1.wireOp",EDGE,"E85.MirrorCS"),sQuery(id+"F1.wireOp",EDGE,"E86.MirrorCS"),sQuery(id+"F1.wireOp",EDGE,"E87.MirrorCS"),sQuery(id+"F1.wireOp",EDGE,"E88.MirrorCS"),sQuery(id+"F1.wireOp",EDGE,"E89.MirrorCS"),sQuery(id+"F1.wireOp",EDGE,"E90.MirrorCS"),sQuery(id+"F1.wireOp",EDGE,"E91.MirrorCS"),sQuery(id+"F1.wireOp",EDGE,"E92.MirrorCS"),sQuery(id+"F1.wireOp",EDGE,"E93.MirrorCS"),sQuery(id+"F1.wireOp",EDGE,"E94.MirrorCS"),sQuery(id+"F1.wireOp",EDGE,"E95.MirrorCS"),sQuery(id+"F1.wireOp",EDGE,"E96.MirrorCS"),sQuery(id+"F1.wireOp",EDGE,"E97.MirrorCS"),sQuery(id+"F1.wireOp",EDGE,"E98.MirrorCS"),sQuery(id+"F1.wireOp",EDGE,"E99.MirrorCS"),sQuery(id+"F1.wireOp",EDGE,"E100.MirrorCS"),sQuery(id+"F1.wireOp",EDGE,"E101.MirrorCS"),sQuery(id+"F1.wireOp",EDGE,"E102.MirrorCS"),sQuery(id+"F1.wireOp",EDGE,"E103.MirrorCS")])],"isStart":false});
            var sketch = newSketch(context, id + "F5", { "sketchPlane" : qUnion([Q0])});
            skLineSegment(sketch, "E110.left", {"start": v(-145, -100) * mm, "end": v(-145, 100) * mm});
            skLineSegment(sketch, "E110.right", {"start": v(-141, -100) * mm, "end": v(-141, 100) * mm});
            skLineSegment(sketch, "E111", {"start": v(-141, -100) * mm, "end": v(-145, -100) * mm});
            skLineSegment(sketch, "E112", {"start": v(-141, 100) * mm, "end": v(-145, 100) * mm});
            skSolve(sketch);
        }
        {
            var Q0;
            Q0 = qSketchRegion(id + "F5", true);
            extrude(context, id + "F6", {"entities" : qUnion([Q0]), "depth" : 100 * mm});
        }
        {
            var Q0;
            Q0=makeQuery(id+"F4.opExtrude","SWEPT_BODY",BODY,{"disambiguationData":[OSD([sQuery(id+"F3.wireOp",EDGE,"E104.bottom"),sQuery(id+"F3.wireOp",EDGE,"E104.top"),sQuery(id+"F3.wireOp",EDGE,"E104.left"),sQuery(id+"F3.wireOp",EDGE,"E104.right")])]});
            var Q1;
            Q1=makeQuery(id+"F4.opExtrude","SWEPT_BODY",BODY,{"disambiguationData":[OSD([sQuery(id+"F3.wireOp",EDGE,"E105.bottom"),sQuery(id+"F3.wireOp",EDGE,"E105.top"),sQuery(id+"F3.wireOp",EDGE,"E105.left"),sQuery(id+"F3.wireOp",EDGE,"E105.right")])]});
            var Q2;
            Q2=makeQuery(id+"F4.opExtrude","SWEPT_BODY",BODY,{"disambiguationData":[OSD([sQuery(id+"F3.wireOp",EDGE,"E106.bottom"),sQuery(id+"F3.wireOp",EDGE,"E106.top"),sQuery(id+"F3.wireOp",EDGE,"E106.left"),sQuery(id+"F3.wireOp",EDGE,"E106.right")])]});
            var Q3;
            Q3=makeQuery(id+"F4.opExtrude","SWEPT_BODY",BODY,{"disambiguationData":[OSD([sQuery(id+"F3.wireOp",EDGE,"E107.bottom"),sQuery(id+"F3.wireOp",EDGE,"E107.top"),sQuery(id+"F3.wireOp",EDGE,"E107.left"),sQuery(id+"F3.wireOp",EDGE,"E107.right")])]});
            var Q4;
            Q4=makeQuery(id+"F4.opExtrude","SWEPT_BODY",BODY,{"disambiguationData":[OSD([sQuery(id+"F3.wireOp",EDGE,"E108.bottom"),sQuery(id+"F3.wireOp",EDGE,"E108.top"),sQuery(id+"F3.wireOp",EDGE,"E108.left"),sQuery(id+"F3.wireOp",EDGE,"E108.right")])]});
            var Q5;
            Q5=makeQuery(id+"F4.opExtrude","SWEPT_BODY",BODY,{"disambiguationData":[OSD([sQuery(id+"F3.wireOp",EDGE,"E109.bottom"),sQuery(id+"F3.wireOp",EDGE,"E109.top"),sQuery(id+"F3.wireOp",EDGE,"E109.left"),sQuery(id+"F3.wireOp",EDGE,"E109.right")])]});
            var Q6;
            Q6=makeQuery(id+"F6.opExtrude","SWEPT_BODY",BODY,{"disambiguationData":[OSD([sQuery(id+"F5.wireOp",EDGE,"E110.bottom"),sQuery(id+"F5.wireOp",EDGE,"E110.top"),sQuery(id+"F5.wireOp",EDGE,"E110.left"),sQuery(id+"F5.wireOp",EDGE,"E110.right")])]});
            booleanBodies(context, id + "F7", {"operationType" : BooleanOperationType.UNION, "tools" : qUnion([Q0, Q1, Q2, Q3, Q4, Q5, Q6])});
        }
        {
            var Q0;
            Q0=makeQuery(id+"F2.opExtrude","CAP_FACE",FACE,{"disambiguationData":[OSD([sQuery(id+"F1.wireOp",EDGE,"E0.bottom"),sQuery(id+"F1.wireOp",EDGE,"E0.top"),sQuery(id+"F1.wireOp",EDGE,"E0.left"),sQuery(id+"F1.wireOp",EDGE,"E0.right"),sQuery(id+"F1.wireOp",EDGE,"E3.bottom"),sQuery(id+"F1.wireOp",EDGE,"E3.top"),sQuery(id+"F1.wireOp",EDGE,"E3.left"),sQuery(id+"F1.wireOp",EDGE,"E3.right"),sQuery(id+"F1.wireOp",EDGE,"E4.1.0.0"),sQuery(id+"F1.wireOp",EDGE,"E4.1.0.1"),sQuery(id+"F1.wireOp",EDGE,"E4.1.0.2"),sQuery(id+"F1.wireOp",EDGE,"E4.1.0.3"),sQuery(id+"F1.wireOp",EDGE,"E4.2.0.0"),sQuery(id+"F1.wireOp",EDGE,"E4.2.0.1"),sQuery(id+"F1.wireOp",EDGE,"E4.2.0.2"),sQuery(id+"F1.wireOp",EDGE,"E4.2.0.3"),sQuery(id+"F1.wireOp",EDGE,"E4.3.0.0"),sQuery(id+"F1.wireOp",EDGE,"E4.3.0.1"),sQuery(id+"F1.wireOp",EDGE,"E4.3.0.2"),sQuery(id+"F1.wireOp",EDGE,"E4.3.0.3"),sQuery(id+"F1.wireOp",EDGE,"E4.4.0.0"),sQuery(id+"F1.wireOp",EDGE,"E4.4.0.1"),sQuery(id+"F1.wireOp",EDGE,"E4.4.0.2"),sQuery(id+"F1.wireOp",EDGE,"E4.4.0.3"),sQuery(id+"F1.wireOp",EDGE,"E5.MirrorCS"),sQuery(id+"F1.wireOp",EDGE,"E6.MirrorCS"),sQuery(id+"F1.wireOp",EDGE,"E7.MirrorCS"),sQuery(id+"F1.wireOp",EDGE,"E8.MirrorCS"),sQuery(id+"F1.wireOp",EDGE,"E9.MirrorCS"),sQuery(id+"F1.wireOp",EDGE,"E10.MirrorCS"),sQuery(id+"F1.wireOp",EDGE,"E11.MirrorCS"),sQuery(id+"F1.wireOp",EDGE,"E12.MirrorCS"),sQuery(id+"F1.wireOp",EDGE,"E13.MirrorCS"),sQuery(id+"F1.wireOp",EDGE,"E14.MirrorCS"),sQuery(id+"F1.wireOp",EDGE,"E15.MirrorCS"),sQuery(id+"F1.wireOp",EDGE,"E16.MirrorCS"),sQuery(id+"F1.wireOp",EDGE,"E17.MirrorCS"),sQuery(id+"F1.wireOp",EDGE,"E18.MirrorCS"),sQuery(id+"F1.wireOp",EDGE,"E19.MirrorCS"),sQuery(id+"F1.wireOp",EDGE,"E20.MirrorCS"),sQuery(id+"F1.wireOp",EDGE,"E21.MirrorCS"),sQuery(id+"F1.wireOp",EDGE,"E23.MirrorCS"),sQuery(id+"F1.wireOp",EDGE,"E24.MirrorCS"),sQuery(id+"F1.wireOp",EDGE,"E25.MirrorCS"),sQuery(id+"F1.wireOp",EDGE,"E26.bottom"),sQuery(id+"F1.wireOp",EDGE,"E26.top"),sQuery(id+"F1.wireOp",EDGE,"E26.left"),sQuery(id+"F1.wireOp",EDGE,"E26.right"),sQuery(id+"F1.wireOp",EDGE,"E27.0.1.0"),sQuery(id+"F1.wireOp",EDGE,"E27.0.1.1"),sQuery(id+"F1.wireOp",EDGE,"E27.0.1.2"),sQuery(id+"F1.wireOp",EDGE,"E27.0.1.3"),sQuery(id+"F1.wireOp",EDGE,"E27.0.2.0"),sQuery(id+"F1.wireOp",EDGE,"E27.0.2.1"),sQuery(id+"F1.wireOp",EDGE,"E27.0.2.2"),sQuery(id+"F1.wireOp",EDGE,"E27.0.2.3"),sQuery(id+"F1.wireOp",EDGE,"E28.MirrorCS"),sQuery(id+"F1.wireOp",EDGE,"E30.MirrorCS"),sQuery(id+"F1.wireOp",EDGE,"E31.MirrorCS"),sQuery(id+"F1.wireOp",EDGE,"E32.MirrorCS"),sQuery(id+"F1.wireOp",EDGE,"E33.MirrorCS"),sQuery(id+"F1.wireOp",EDGE,"E29.MirrorCS"),sQuery(id+"F1.wireOp",EDGE,"E34.MirrorCS"),sQuery(id+"F1.wireOp",EDGE,"E35.MirrorCS"),sQuery(id+"F1.wireOp",EDGE,"E36.MirrorCS"),sQuery(id+"F1.wireOp",EDGE,"E37.MirrorCS"),sQuery(id+"F1.wireOp",EDGE,"E38.MirrorCS"),sQuery(id+"F1.wireOp",EDGE,"E39.MirrorCS"),sQuery(id+"F1.wireOp",EDGE,"E40.MirrorCS"),sQuery(id+"F1.wireOp",EDGE,"E41.MirrorCS"),sQuery(id+"F1.wireOp",EDGE,"E42.MirrorCS"),sQuery(id+"F1.wireOp",EDGE,"E43.MirrorCS"),sQuery(id+"F1.wireOp",EDGE,"E44.MirrorCS"),sQuery(id+"F1.wireOp",EDGE,"E45.MirrorCS"),sQuery(id+"F1.wireOp",EDGE,"E46.MirrorCS"),sQuery(id+"F1.wireOp",EDGE,"E47.MirrorCS"),sQuery(id+"F1.wireOp",EDGE,"E48.MirrorCS"),sQuery(id+"F1.wireOp",EDGE,"E49.MirrorCS"),sQuery(id+"F1.wireOp",EDGE,"E50.MirrorCS"),sQuery(id+"F1.wireOp",EDGE,"E51.MirrorCS"),sQuery(id+"F1.wireOp",EDGE,"E52.MirrorCS"),sQuery(id+"F1.wireOp",EDGE,"E53.MirrorCS"),sQuery(id+"F1.wireOp",EDGE,"E54.MirrorCS"),sQuery(id+"F1.wireOp",EDGE,"E55.MirrorCS"),sQuery(id+"F1.wireOp",EDGE,"E56.MirrorCS"),sQuery(id+"F1.wireOp",EDGE,"E57.MirrorCS"),sQuery(id+"F1.wireOp",EDGE,"E58.MirrorCS"),sQuery(id+"F1.wireOp",EDGE,"E59.MirrorCS"),sQuery(id+"F1.wireOp",EDGE,"E60.MirrorCS"),sQuery(id+"F1.wireOp",EDGE,"E61.MirrorCS"),sQuery(id+"F1.wireOp",EDGE,"E62.MirrorCS"),sQuery(id+"F1.wireOp",EDGE,"E63.MirrorCS"),sQuery(id+"F1.wireOp",EDGE,"E64.MirrorCS"),sQuery(id+"F1.wireOp",EDGE,"E65.MirrorCS"),sQuery(id+"F1.wireOp",EDGE,"E66.MirrorCS"),sQuery(id+"F1.wireOp",EDGE,"E67.MirrorCS"),sQuery(id+"F1.wireOp",EDGE,"E68.MirrorCS"),sQuery(id+"F1.wireOp",EDGE,"E69.MirrorCS"),sQuery(id+"F1.wireOp",EDGE,"E70.MirrorCS"),sQuery(id+"F1.wireOp",EDGE,"E71.MirrorCS"),sQuery(id+"F1.wireOp",EDGE,"E72.MirrorCS"),sQuery(id+"F1.wireOp",EDGE,"E73.MirrorCS"),sQuery(id+"F1.wireOp",EDGE,"E74.MirrorCS"),sQuery(id+"F1.wireOp",EDGE,"E75.MirrorCS"),sQuery(id+"F1.wireOp",EDGE,"E76.MirrorCS"),sQuery(id+"F1.wireOp",EDGE,"E77.MirrorCS"),sQuery(id+"F1.wireOp",EDGE,"E78.MirrorCS"),sQuery(id+"F1.wireOp",EDGE,"E79.MirrorCS"),sQuery(id+"F1.wireOp",EDGE,"E80.MirrorCS"),sQuery(id+"F1.wireOp",EDGE,"E81.MirrorCS"),sQuery(id+"F1.wireOp",EDGE,"E82.MirrorCS"),sQuery(id+"F1.wireOp",EDGE,"E83.MirrorCS"),sQuery(id+"F1.wireOp",EDGE,"E84.MirrorCS"),sQuery(id+"F1.wireOp",EDGE,"E85.MirrorCS"),sQuery(id+"F1.wireOp",EDGE,"E86.MirrorCS"),sQuery(id+"F1.wireOp",EDGE,"E87.MirrorCS"),sQuery(id+"F1.wireOp",EDGE,"E88.MirrorCS"),sQuery(id+"F1.wireOp",EDGE,"E89.MirrorCS"),sQuery(id+"F1.wireOp",EDGE,"E90.MirrorCS"),sQuery(id+"F1.wireOp",EDGE,"E91.MirrorCS"),sQuery(id+"F1.wireOp",EDGE,"E92.MirrorCS"),sQuery(id+"F1.wireOp",EDGE,"E93.MirrorCS"),sQuery(id+"F1.wireOp",EDGE,"E94.MirrorCS"),sQuery(id+"F1.wireOp",EDGE,"E95.MirrorCS"),sQuery(id+"F1.wireOp",EDGE,"E96.MirrorCS"),sQuery(id+"F1.wireOp",EDGE,"E97.MirrorCS"),sQuery(id+"F1.wireOp",EDGE,"E98.MirrorCS"),sQuery(id+"F1.wireOp",EDGE,"E99.MirrorCS"),sQuery(id+"F1.wireOp",EDGE,"E100.MirrorCS"),sQuery(id+"F1.wireOp",EDGE,"E101.MirrorCS"),sQuery(id+"F1.wireOp",EDGE,"E102.MirrorCS"),sQuery(id+"F1.wireOp",EDGE,"E103.MirrorCS")])],"isStart":false});
            var sketch = newSketch(context, id + "F8", { "sketchPlane" : qUnion([Q0])});
            skLineSegment(sketch, "E113.bottom", {"start": v(-140, 90) * mm, "end": v(-125, 90) * mm});
            skLineSegment(sketch, "E113.top", {"start": v(-140, 86) * mm, "end": v(-125, 86) * mm});
            skLineSegment(sketch, "E113.left", {"start": v(-140, 90) * mm, "end": v(-140, 86) * mm});
            skLineSegment(sketch, "E113.right", {"start": v(-125, 90) * mm, "end": v(-125, 86) * mm});
            skLineSegment(sketch, "E114.bottom", {"start": v(-110, 90) * mm, "end": v(-95, 90) * mm});
            skLineSegment(sketch, "E114.top", {"start": v(-110, 86) * mm, "end": v(-95, 86) * mm});
            skLineSegment(sketch, "E114.left", {"start": v(-110, 90) * mm, "end": v(-110, 86) * mm});
            skLineSegment(sketch, "E114.right", {"start": v(-95, 90) * mm, "end": v(-95, 86) * mm});
            skLineSegment(sketch, "E115.bottom", {"start": v(-80, 90) * mm, "end": v(-65, 90) * mm});
            skLineSegment(sketch, "E115.top", {"start": v(-80, 86) * mm, "end": v(-65, 86) * mm});
            skLineSegment(sketch, "E115.left", {"start": v(-80, 90) * mm, "end": v(-80, 86) * mm});
            skLineSegment(sketch, "E115.right", {"start": v(-65, 90) * mm, "end": v(-65, 86) * mm});
            skLineSegment(sketch, "E116.bottom", {"start": v(-50, 90) * mm, "end": v(-35, 90) * mm});
            skLineSegment(sketch, "E116.top", {"start": v(-50, 86) * mm, "end": v(-35, 86) * mm});
            skLineSegment(sketch, "E116.left", {"start": v(-50, 90) * mm, "end": v(-50, 86) * mm});
            skLineSegment(sketch, "E116.right", {"start": v(-35, 90) * mm, "end": v(-35, 86) * mm});
            skLineSegment(sketch, "E117.bottom", {"start": v(-20, 90) * mm, "end": v(-5, 90) * mm});
            skLineSegment(sketch, "E117.top", {"start": v(-20, 86) * mm, "end": v(-5, 86) * mm});
            skLineSegment(sketch, "E117.left", {"start": v(-20, 90) * mm, "end": v(-20, 86) * mm});
            skLineSegment(sketch, "E117.right", {"start": v(-5, 90) * mm, "end": v(-5, 86) * mm});
            skLineSegment(sketch, "E118.bottom", {"start": v(5, 90) * mm, "end": v(20, 90) * mm});
            skLineSegment(sketch, "E118.top", {"start": v(5, 86) * mm, "end": v(20, 86) * mm});
            skLineSegment(sketch, "E118.left", {"start": v(5, 90) * mm, "end": v(5, 86) * mm});
            skLineSegment(sketch, "E118.right", {"start": v(20, 90) * mm, "end": v(20, 86) * mm});
            skLineSegment(sketch, "E119.bottom", {"start": v(35, 90) * mm, "end": v(50, 90) * mm});
            skLineSegment(sketch, "E119.top", {"start": v(35, 86) * mm, "end": v(50, 86) * mm});
            skLineSegment(sketch, "E119.left", {"start": v(35, 90) * mm, "end": v(35, 86) * mm});
            skLineSegment(sketch, "E119.right", {"start": v(50, 90) * mm, "end": v(50, 86) * mm});
            skLineSegment(sketch, "E120.bottom", {"start": v(65, 90) * mm, "end": v(80, 90) * mm});
            skLineSegment(sketch, "E120.top", {"start": v(65, 86) * mm, "end": v(80, 86) * mm});
            skLineSegment(sketch, "E120.left", {"start": v(65, 90) * mm, "end": v(65, 86) * mm});
            skLineSegment(sketch, "E120.right", {"start": v(80, 90) * mm, "end": v(80, 86) * mm});
            skLineSegment(sketch, "E121.bottom", {"start": v(95, 90) * mm, "end": v(110, 90) * mm});
            skLineSegment(sketch, "E121.top", {"start": v(95, 86) * mm, "end": v(110, 86) * mm});
            skLineSegment(sketch, "E121.left", {"start": v(95, 90) * mm, "end": v(95, 86) * mm});
            skLineSegment(sketch, "E121.right", {"start": v(110, 90) * mm, "end": v(110, 86) * mm});
            skLineSegment(sketch, "E122.bottom", {"start": v(125, 90) * mm, "end": v(140, 90) * mm});
            skLineSegment(sketch, "E122.top", {"start": v(125, 86) * mm, "end": v(140, 86) * mm});
            skLineSegment(sketch, "E122.left", {"start": v(125, 90) * mm, "end": v(125, 86) * mm});
            skLineSegment(sketch, "E122.right", {"start": v(140, 90) * mm, "end": v(140, 86) * mm});
            skSolve(sketch);
        }
        {
            var Q0;
            Q0 = qSketchRegion(id + "F8", true);
            extrude(context, id + "F9", {"entities" : qUnion([Q0]), "oppositeDirection" : true, "depth" : 4 * mm});
        }
        {
            var Q0;
            Q0=makeQuery(id+"F2.opExtrude","CAP_FACE",FACE,{"disambiguationData":[OSD([sQuery(id+"F1.wireOp",EDGE,"E0.bottom"),sQuery(id+"F1.wireOp",EDGE,"E0.top"),sQuery(id+"F1.wireOp",EDGE,"E0.left"),sQuery(id+"F1.wireOp",EDGE,"E0.right"),sQuery(id+"F1.wireOp",EDGE,"E3.bottom"),sQuery(id+"F1.wireOp",EDGE,"E3.top"),sQuery(id+"F1.wireOp",EDGE,"E3.left"),sQuery(id+"F1.wireOp",EDGE,"E3.right"),sQuery(id+"F1.wireOp",EDGE,"E4.1.0.0"),sQuery(id+"F1.wireOp",EDGE,"E4.1.0.1"),sQuery(id+"F1.wireOp",EDGE,"E4.1.0.2"),sQuery(id+"F1.wireOp",EDGE,"E4.1.0.3"),sQuery(id+"F1.wireOp",EDGE,"E4.2.0.0"),sQuery(id+"F1.wireOp",EDGE,"E4.2.0.1"),sQuery(id+"F1.wireOp",EDGE,"E4.2.0.2"),sQuery(id+"F1.wireOp",EDGE,"E4.2.0.3"),sQuery(id+"F1.wireOp",EDGE,"E4.3.0.0"),sQuery(id+"F1.wireOp",EDGE,"E4.3.0.1"),sQuery(id+"F1.wireOp",EDGE,"E4.3.0.2"),sQuery(id+"F1.wireOp",EDGE,"E4.3.0.3"),sQuery(id+"F1.wireOp",EDGE,"E4.4.0.0"),sQuery(id+"F1.wireOp",EDGE,"E4.4.0.1"),sQuery(id+"F1.wireOp",EDGE,"E4.4.0.2"),sQuery(id+"F1.wireOp",EDGE,"E4.4.0.3"),sQuery(id+"F1.wireOp",EDGE,"E5.MirrorCS"),sQuery(id+"F1.wireOp",EDGE,"E6.MirrorCS"),sQuery(id+"F1.wireOp",EDGE,"E7.MirrorCS"),sQuery(id+"F1.wireOp",EDGE,"E8.MirrorCS"),sQuery(id+"F1.wireOp",EDGE,"E9.MirrorCS"),sQuery(id+"F1.wireOp",EDGE,"E10.MirrorCS"),sQuery(id+"F1.wireOp",EDGE,"E11.MirrorCS"),sQuery(id+"F1.wireOp",EDGE,"E12.MirrorCS"),sQuery(id+"F1.wireOp",EDGE,"E13.MirrorCS"),sQuery(id+"F1.wireOp",EDGE,"E14.MirrorCS"),sQuery(id+"F1.wireOp",EDGE,"E15.MirrorCS"),sQuery(id+"F1.wireOp",EDGE,"E16.MirrorCS"),sQuery(id+"F1.wireOp",EDGE,"E17.MirrorCS"),sQuery(id+"F1.wireOp",EDGE,"E18.MirrorCS"),sQuery(id+"F1.wireOp",EDGE,"E19.MirrorCS"),sQuery(id+"F1.wireOp",EDGE,"E20.MirrorCS"),sQuery(id+"F1.wireOp",EDGE,"E21.MirrorCS"),sQuery(id+"F1.wireOp",EDGE,"E23.MirrorCS"),sQuery(id+"F1.wireOp",EDGE,"E24.MirrorCS"),sQuery(id+"F1.wireOp",EDGE,"E25.MirrorCS"),sQuery(id+"F1.wireOp",EDGE,"E26.bottom"),sQuery(id+"F1.wireOp",EDGE,"E26.top"),sQuery(id+"F1.wireOp",EDGE,"E26.left"),sQuery(id+"F1.wireOp",EDGE,"E26.right"),sQuery(id+"F1.wireOp",EDGE,"E27.0.1.0"),sQuery(id+"F1.wireOp",EDGE,"E27.0.1.1"),sQuery(id+"F1.wireOp",EDGE,"E27.0.1.2"),sQuery(id+"F1.wireOp",EDGE,"E27.0.1.3"),sQuery(id+"F1.wireOp",EDGE,"E27.0.2.0"),sQuery(id+"F1.wireOp",EDGE,"E27.0.2.1"),sQuery(id+"F1.wireOp",EDGE,"E27.0.2.2"),sQuery(id+"F1.wireOp",EDGE,"E27.0.2.3"),sQuery(id+"F1.wireOp",EDGE,"E28.MirrorCS"),sQuery(id+"F1.wireOp",EDGE,"E30.MirrorCS"),sQuery(id+"F1.wireOp",EDGE,"E31.MirrorCS"),sQuery(id+"F1.wireOp",EDGE,"E32.MirrorCS"),sQuery(id+"F1.wireOp",EDGE,"E33.MirrorCS"),sQuery(id+"F1.wireOp",EDGE,"E29.MirrorCS"),sQuery(id+"F1.wireOp",EDGE,"E34.MirrorCS"),sQuery(id+"F1.wireOp",EDGE,"E35.MirrorCS"),sQuery(id+"F1.wireOp",EDGE,"E36.MirrorCS"),sQuery(id+"F1.wireOp",EDGE,"E37.MirrorCS"),sQuery(id+"F1.wireOp",EDGE,"E38.MirrorCS"),sQuery(id+"F1.wireOp",EDGE,"E39.MirrorCS"),sQuery(id+"F1.wireOp",EDGE,"E40.MirrorCS"),sQuery(id+"F1.wireOp",EDGE,"E41.MirrorCS"),sQuery(id+"F1.wireOp",EDGE,"E42.MirrorCS"),sQuery(id+"F1.wireOp",EDGE,"E43.MirrorCS"),sQuery(id+"F1.wireOp",EDGE,"E44.MirrorCS"),sQuery(id+"F1.wireOp",EDGE,"E45.MirrorCS"),sQuery(id+"F1.wireOp",EDGE,"E46.MirrorCS"),sQuery(id+"F1.wireOp",EDGE,"E47.MirrorCS"),sQuery(id+"F1.wireOp",EDGE,"E48.MirrorCS"),sQuery(id+"F1.wireOp",EDGE,"E49.MirrorCS"),sQuery(id+"F1.wireOp",EDGE,"E50.MirrorCS"),sQuery(id+"F1.wireOp",EDGE,"E51.MirrorCS"),sQuery(id+"F1.wireOp",EDGE,"E52.MirrorCS"),sQuery(id+"F1.wireOp",EDGE,"E53.MirrorCS"),sQuery(id+"F1.wireOp",EDGE,"E54.MirrorCS"),sQuery(id+"F1.wireOp",EDGE,"E55.MirrorCS"),sQuery(id+"F1.wireOp",EDGE,"E56.MirrorCS"),sQuery(id+"F1.wireOp",EDGE,"E57.MirrorCS"),sQuery(id+"F1.wireOp",EDGE,"E58.MirrorCS"),sQuery(id+"F1.wireOp",EDGE,"E59.MirrorCS"),sQuery(id+"F1.wireOp",EDGE,"E60.MirrorCS"),sQuery(id+"F1.wireOp",EDGE,"E61.MirrorCS"),sQuery(id+"F1.wireOp",EDGE,"E62.MirrorCS"),sQuery(id+"F1.wireOp",EDGE,"E63.MirrorCS"),sQuery(id+"F1.wireOp",EDGE,"E64.MirrorCS"),sQuery(id+"F1.wireOp",EDGE,"E65.MirrorCS"),sQuery(id+"F1.wireOp",EDGE,"E66.MirrorCS"),sQuery(id+"F1.wireOp",EDGE,"E67.MirrorCS"),sQuery(id+"F1.wireOp",EDGE,"E68.MirrorCS"),sQuery(id+"F1.wireOp",EDGE,"E69.MirrorCS"),sQuery(id+"F1.wireOp",EDGE,"E70.MirrorCS"),sQuery(id+"F1.wireOp",EDGE,"E71.MirrorCS"),sQuery(id+"F1.wireOp",EDGE,"E72.MirrorCS"),sQuery(id+"F1.wireOp",EDGE,"E73.MirrorCS"),sQuery(id+"F1.wireOp",EDGE,"E74.MirrorCS"),sQuery(id+"F1.wireOp",EDGE,"E75.MirrorCS"),sQuery(id+"F1.wireOp",EDGE,"E76.MirrorCS"),sQuery(id+"F1.wireOp",EDGE,"E77.MirrorCS"),sQuery(id+"F1.wireOp",EDGE,"E78.MirrorCS"),sQuery(id+"F1.wireOp",EDGE,"E79.MirrorCS"),sQuery(id+"F1.wireOp",EDGE,"E80.MirrorCS"),sQuery(id+"F1.wireOp",EDGE,"E81.MirrorCS"),sQuery(id+"F1.wireOp",EDGE,"E82.MirrorCS"),sQuery(id+"F1.wireOp",EDGE,"E83.MirrorCS"),sQuery(id+"F1.wireOp",EDGE,"E84.MirrorCS"),sQuery(id+"F1.wireOp",EDGE,"E85.MirrorCS"),sQuery(id+"F1.wireOp",EDGE,"E86.MirrorCS"),sQuery(id+"F1.wireOp",EDGE,"E87.MirrorCS"),sQuery(id+"F1.wireOp",EDGE,"E88.MirrorCS"),sQuery(id+"F1.wireOp",EDGE,"E89.MirrorCS"),sQuery(id+"F1.wireOp",EDGE,"E90.MirrorCS"),sQuery(id+"F1.wireOp",EDGE,"E91.MirrorCS"),sQuery(id+"F1.wireOp",EDGE,"E92.MirrorCS"),sQuery(id+"F1.wireOp",EDGE,"E93.MirrorCS"),sQuery(id+"F1.wireOp",EDGE,"E94.MirrorCS"),sQuery(id+"F1.wireOp",EDGE,"E95.MirrorCS"),sQuery(id+"F1.wireOp",EDGE,"E96.MirrorCS"),sQuery(id+"F1.wireOp",EDGE,"E97.MirrorCS"),sQuery(id+"F1.wireOp",EDGE,"E98.MirrorCS"),sQuery(id+"F1.wireOp",EDGE,"E99.MirrorCS"),sQuery(id+"F1.wireOp",EDGE,"E100.MirrorCS"),sQuery(id+"F1.wireOp",EDGE,"E101.MirrorCS"),sQuery(id+"F1.wireOp",EDGE,"E102.MirrorCS"),sQuery(id+"F1.wireOp",EDGE,"E103.MirrorCS")])],"isStart":false});
            var sketch = newSketch(context, id + "F10", { "sketchPlane" : qUnion([Q0])});
            skLineSegment(sketch, "E123.bottom", {"start": v(-141, 86) * mm, "end": v(140, 86) * mm});
            skLineSegment(sketch, "E123.top", {"start": v(-141, 90) * mm, "end": v(140, 90) * mm});
            skLineSegment(sketch, "E123.left", {"start": v(-141, 86) * mm, "end": v(-141, 90) * mm});
            skLineSegment(sketch, "E123.right", {"start": v(140, 86) * mm, "end": v(140, 100) * mm});
            skSolve(sketch);
        }
        {
            var Q0;
            Q0 = qSketchRegion(id + "F10", true);
            extrude(context, id + "F11", {"entities" : qUnion([Q0]), "depth" : 100 * mm});
        }
    });
